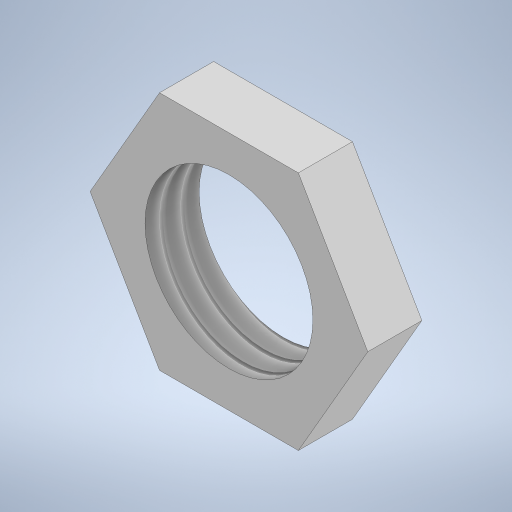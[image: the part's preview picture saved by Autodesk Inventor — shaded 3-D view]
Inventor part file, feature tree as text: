
AUTODESK INVENTOR PART (.ipt)
format: ipt  version: 2023 (Build 270158000, 158)  size: 238,080 bytes
history: native  units: in
note: dims shown in document units (in); Inventor stores cm internally (conversion verified against a paired STEP export)
features: sketch x2, extrude x1, hole x1
ambient origin geometry x8: Origin, YZ Plane, XZ Plane, XY Plane, X Axis, Y Axis, Z Axis, Center Point
bodies: Solid1 (feature_tree)
feature tree (4):
  extrude  "Extrusion1"  Depth=0.0709in TaperAngle=0.0deg
  hole  "Hole1"  [1 undecoded]
  sketch  "Sketch1"  dims[d0=0.315in d1=0.0709in d2=0.0in]
  sketch  "Sketch2"  dims[d3=0.22in d4=0.5in d5=0.1575in d6=0.0787in d7=90.0deg d8=0.315in d9=0.8108in]
note: 1 required parameter value undecoded (feature->parameter linkage not recoverable at this tier; creation-order binding heuristic only, values carry confidence <= 0.55)
